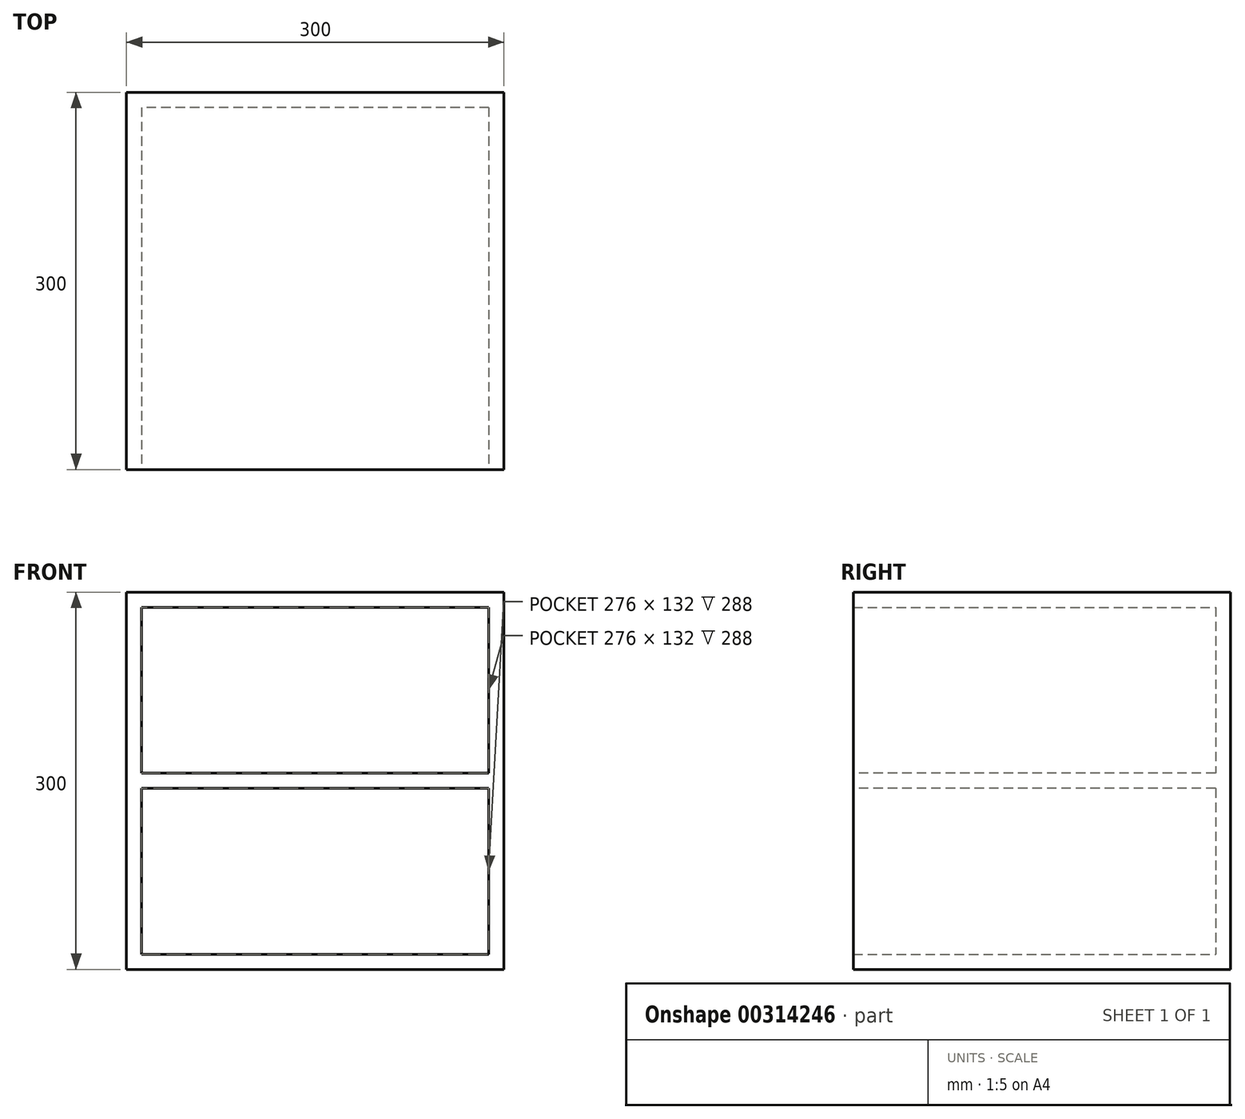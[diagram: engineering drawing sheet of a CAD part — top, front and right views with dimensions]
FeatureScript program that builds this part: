
annotation { "Feature Type Name" : "Feature", "Feature Type Description" : "" }
export const myFeature = defineFeature(function(context is Context, id is Id, definition is map)
    precondition{}
    {
        {
            var Q0;
            Q0=qCreatedBy(makeId("Front.planeOp"),FACE);
            var sketch = newSketch(context, id + "F0", { "sketchPlane" : qUnion([Q0])});
            skLineSegment(sketch, "E0.bottom", {"start": v(-150, 150) * mm, "end": v(150, 150) * mm});
            skLineSegment(sketch, "E0.top", {"start": v(-150, -150) * mm, "end": v(150, -150) * mm});
            skLineSegment(sketch, "E0.left", {"start": v(-150, 150) * mm, "end": v(-150, -150) * mm});
            skLineSegment(sketch, "E0.right", {"start": v(150, 150) * mm, "end": v(150, -150) * mm});
            skPoint(sketch, "E0.middle", {"position": v(0, 0) * mm});
            skSolve(sketch);
        }
        {
            var Q0;
            Q0=makeQuery(id+"F0.imprint","IMPRINT",FACE,{"disambiguationData":[TD([[makeQuery(id+"F0.imprint","IMPRINT",EDGE,{"derivedFrom":sQuery(id+"F0.wireOp",EDGE,"E0.bottom")}),-1.0]])]});
            extrude(context, id + "F1", {"entities" : qUnion([Q0]), "endBound" : BoundingType.SYMMETRIC, "depth" : 300 * mm});
        }
        {
            var Q0;
            Q0=makeQuery(id+"F1.opExtrude","CAP_FACE",FACE,{"disambiguationData":[OSD([sQuery(id+"F0.wireOp",EDGE,"E0.bottom"),sQuery(id+"F0.wireOp",EDGE,"E0.top"),sQuery(id+"F0.wireOp",EDGE,"E0.left"),sQuery(id+"F0.wireOp",EDGE,"E0.right")])],"isStart":false});
            shell(context, id + "F2", {"entities" : qUnion([Q0]), "thickness" : 12 * mm});
        }
        {
            var Q0;
            Q0=makeQuery(id+"F1.opExtrude","CAP_FACE",FACE,{"disambiguationData":[OSD([sQuery(id+"F0.wireOp",EDGE,"E0.bottom"),sQuery(id+"F0.wireOp",EDGE,"E0.top"),sQuery(id+"F0.wireOp",EDGE,"E0.left"),sQuery(id+"F0.wireOp",EDGE,"E0.right")])],"isStart":false});
            var sketch = newSketch(context, id + "F3", { "sketchPlane" : qUnion([Q0])});
            skLineSegment(sketch, "E1.bottom", {"start": v(144, 6) * mm, "end": v(-144, 6) * mm});
            skLineSegment(sketch, "E1.top", {"start": v(144, -6) * mm, "end": v(-144, -6) * mm});
            skLineSegment(sketch, "E1.left", {"start": v(144, 6) * mm, "end": v(144, -6) * mm});
            skLineSegment(sketch, "E1.right", {"start": v(-144, 6) * mm, "end": v(-144, -6) * mm});
            skPoint(sketch, "E1.middle", {"position": v(0, 0) * mm});
            skSolve(sketch);
        }
        {
            var Q0;
            {var subQ0=sQuery(id+"F3.wireOp",EDGE,"E1.bottom");var subQ1=sQuery(id+"F0.wireOp",EDGE,"E0.right");var subQ2=makeQuery(id+"F2.opShell","OFFSET_EDGE",EDGE,{"disambiguationData":[OSD([subQ1]),TDD([makeQuery(id+"F1.opExtrude","CAP_EDGE",EDGE,{"disambiguationData":[OSD([subQ1])],"isStart":false})])]});var subQ3=makeQuery(id+"F3.imprint","INTERSECT",VERTEX,{"derivedFrom":[subQ2,subQ0]});Q0=makeQuery(id+"F3.imprint","IMPRINT",FACE,{"disambiguationData":[TD([[makeQuery(id+"F3.imprint","IMPRINT",EDGE,{"disambiguationData":[TD([[subQ3,-1.0]])],"derivedFrom":subQ0}),1.0]])]});}
            extrude(context, id + "F4", {"entities" : qUnion([Q0]), "operationType" : NewBodyOperationType.ADD, "oppositeDirection" : true, "depth" : 288 * mm});
        }
    });
